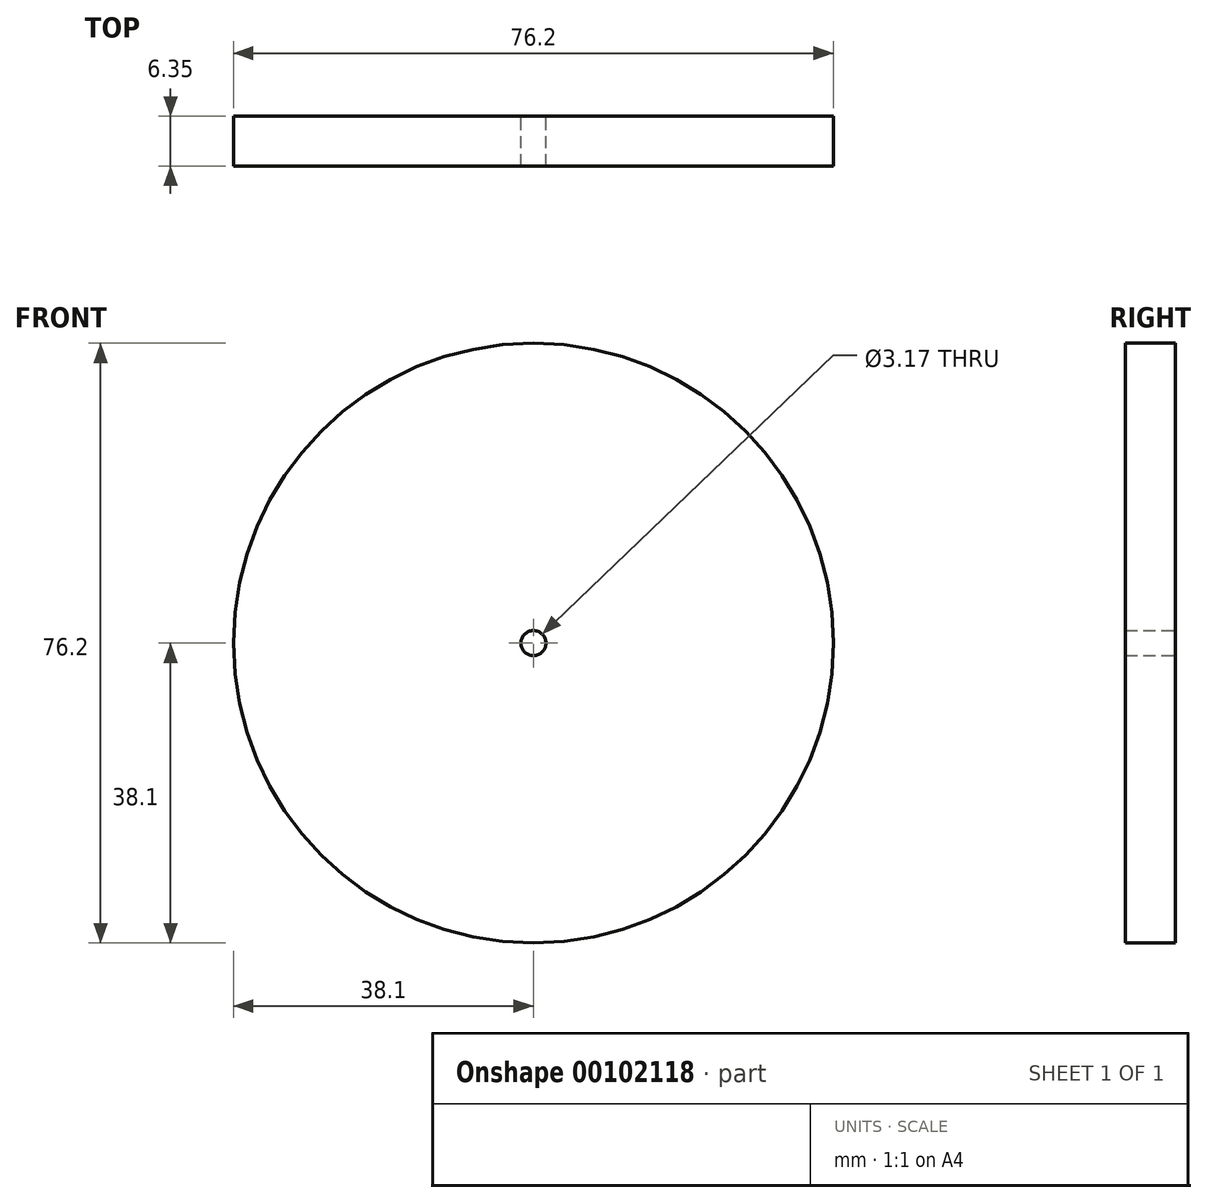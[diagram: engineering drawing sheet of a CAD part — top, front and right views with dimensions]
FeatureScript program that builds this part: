
annotation { "Feature Type Name" : "Feature", "Feature Type Description" : "" }
export const myFeature = defineFeature(function(context is Context, id is Id, definition is map)
    precondition{}
    {
        {
            var Q0;
            Q0=qCreatedBy(makeId("Front.planeOp"),FACE);
            var sketch = newSketch(context, id + "F0", { "sketchPlane" : qUnion([Q0])});
            skCircle(sketch, "E0", {"center": v(0, 0) * mm, "radius": 38.1 * mm});
            skCircle(sketch, "E1", {"center": v(0, 0) * mm, "radius": 1.59 * mm});
            skSolve(sketch);
        }
        {
            var Q0;
            Q0 = qSketchRegion(id + "F0", true);
            extrude(context, id + "F1", {"entities" : qUnion([Q0]), "depth" : 6.35 * mm});
        }
    });
